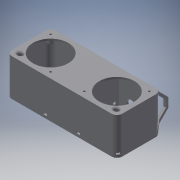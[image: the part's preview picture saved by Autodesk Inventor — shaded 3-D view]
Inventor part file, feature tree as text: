
AUTODESK INVENTOR PART (.ipt)
format: ipt  version: 2016 (Build 200138000, 138)  size: 859,648 bytes
history: native  units: mm
features: sketch x23, extrude x20, projected_geometry x20, reference x10, mirror x4, hole x3, fillet x3, plane x3, chamfer x1
ambient origin geometry x8: Origin, YZ Plane, XZ Plane, XY Plane, X Axis, Y Axis, Z Axis, Center Point
bodies: Solid1 (feature_tree)
feature tree (87):
  extrude  "Extrusion1"  Depth=100.0mm
  extrude  "Extrusion2"  Depth=80.0mm
  extrude  "Extrusion3"  Depth=50.0mm
  hole  "Hole1"  [1 undecoded]
  extrude  "Extrusion4"  Depth=100.0mm
  extrude  "Extrusion5"  Depth=92.0mm
  mirror  "Mirror1"
  fillet  "Fillet1"  Radius=80.0mm
  extrude  "Extrusion6"  TaperAngle=45.0deg  [1 undecoded]
  extrude  "Extrusion7"  Depth=15.0mm
  extrude  "Extrusion8"  Depth=10.0mm TaperAngle=0.0deg
  mirror  "Mirror2"
  plane  "Work Plane1"
  extrude  "Extrusion9"  Depth=7.0mm
  extrude  "Extrusion10"  Depth=12.0mm
  hole  "Hole2"  [1 undecoded]
  mirror  "Mirror3"
  extrude  "Extrusion11"  Depth=5.0mm TaperAngle=0.0deg
  extrude  "Extrusion12"  Depth=15.0mm
  extrude  "Extrusion13"  Depth=3.0mm
  hole  "Hole3"  [1 undecoded]
  plane  "Work Plane2"
  extrude  "Extrusion14"  Depth=38.0mm TaperAngle=0.0deg
  extrude  "Extrusion15"  Depth=10.0mm
  extrude  "Extrusion16"  Depth=10.0mm
  extrude  "Extrusion17"  Depth=7.0mm
  extrude  "Extrusion18"  Depth=7.5mm
  extrude  "Extrusion19"  Depth=7.5mm
  plane  "Work Plane3"
  extrude  "Extrusion20"  Depth=7.0mm
  mirror  "Mirror4"
  chamfer  "Chamfer2"  Distance=10.5mm
  fillet  "Fillet3"  Radius=7.5mm
  fillet  "Fillet4"  Radius=7.0mm
  sketch  "Sketch1"  dims[d0=250.0mm d1=100.0mm]
  sketch  "Sketch2"  dims[d2=4.0mm d3=0.0mm d4=80.0mm]
  sketch  "Sketch3"  dims[d5=80.0mm d6=50.0mm]
  projected_geometry  "Projected Loop1"
  sketch  "Sketch4"  dims[d7=50.0mm d8=4.0mm d9=0.0mm]
  projected_geometry  "Projected Loop2"
  sketch  "Sketch5"  dims[d10=250.0mm d11=100.0mm]
  projected_geometry  "Projected Loop3"
  sketch  "Sketch6"  dims[d12=242.0mm d13=92.0mm d14=80.0mm d15=0.0mm]
  projected_geometry  "Projected Loop4"
  projected_geometry  "Projected Loop5"
  sketch  "Sketch7"  dims[d16=104.0mm d17=45.0deg]
  projected_geometry  "Projected Loop6"
  sketch  "Sketch8"  dims[d18=4.5mm d19=6.0mm d20=4.0mm d21=2.0mm d22=90.0deg d23=8.0mm d24=20.594885mm d25=15.0mm]
  projected_geometry  "Projected Loop7"
  sketch  "Sketch9"  dims[d26=15.0mm d27=10.0mm d28=0.0mm]
  projected_geometry  "Projected Loop8"
  sketch  "Sketch10"  dims[d29=7.0mm d30=7.0mm]
  projected_geometry  "Projected Loop9"
  projected_geometry  "Projected Loop10"
  projected_geometry  "Projected Loop11"
  sketch  "Sketch11"  dims[d31=5.0mm d32=0.0mm d33=12.0mm]
  projected_geometry  "Projected Loop12"
  sketch  "Sketch12"  dims[d34=6.0mm d35=1.0mm]
  sketch  "Sketch13"  dims[d36=4.0mm d37=5.0mm d38=0.0mm]
  sketch  "Sketch14"  dims[d39=15.0mm d40=15.0mm]
  projected_geometry  "Projected Loop13"
  sketch  "Sketch15"  dims[d41=45.0deg d42=3.0mm]
  reference  "Reference1"
  reference  "Reference2"
  reference  "Reference3"
  reference  "Reference4"
  projected_geometry  "Projected Loop14"
  sketch  "Sketch16"  dims[d43=15.0mm d44=55.0mm d45=0.0mm]
  projected_geometry  "Projected Loop15"
  projected_geometry  "Projected Loop16"
  projected_geometry  "Projected Loop17"
  projected_geometry  "Projected Loop18"
  sketch  "Sketch17"  dims[d46=10.0mm d47=38.0mm d48=0.0mm]
  projected_geometry  "Projected Loop19"
  projected_geometry  "Projected Loop20"
  sketch  "Sketch18"  dims[d49=-10.0mm d50=10.0mm]
  reference  "Reference5"
  reference  "Reference6"
  reference  "Reference7"
  reference  "Reference8"
  reference  "Reference9"
  reference  "Reference10"
  sketch  "Sketch19"  dims[d51=15.0mm d52=10.0mm]
  sketch  "Sketch20"  dims[d53=10.0mm d54=0.0mm d55=7.0mm]
  sketch  "Sketch21"  dims[d56=7.5mm d57=7.5mm]
  sketch  "Sketch22"  dims[d58=7.0mm d59=7.5mm]
  sketch  "Sketch23"  dims[d60=7.5mm d61=7.0mm d63=10.5mm d64=7.5mm d65=7.0mm d66=4.0mm d67=0.0mm d68=4.5mm d69=6.0mm d70=4.0mm d71=2.0mm d72=90.0deg d73=8.0mm d74=20.594885mm d75=142.0mm d76=43.0mm d77=20.5mm d78=0.0mm d79=10.0mm d80=21.0mm d81=0.0mm d82=10.0mm d83=0.0mm d84=3.5mm d85=6.0mm d86=4.0mm d87=2.0mm d88=90.0deg d89=10.0mm d90=0.0mm d91=-6.0mm d92=5.7mm d93=5.7mm d94=5.7mm d95=5.7mm d96=2.5mm d97=0.0mm d98=9.5mm d99=6.0mm d100=5.75mm d101=0.0mm d102=8.0mm d103=29.0mm d104=5.75mm d105=0.0mm d106=6.0mm d107=76.25mm d108=0.0mm d109=20.25mm d110=23.5mm d111=0.0mm d113=20.25mm d114=7.0mm d115=23.5mm d116=0.0mm d117=40.0mm d118=135.0deg d119=3.0mm d120=40.0mm d121=135.0deg d122=3.0mm d123=8.0mm d124=5.0mm d125=8.0mm d126=5.0mm d127=8.0mm d128=0.0mm d132=8.0mm d133=2.0mm d134=45.0deg d135=5.0mm d136=3.0mm]
note: 4 required parameter values undecoded (feature->parameter linkage not recoverable at this tier; creation-order binding heuristic only, values carry confidence <= 0.55)
